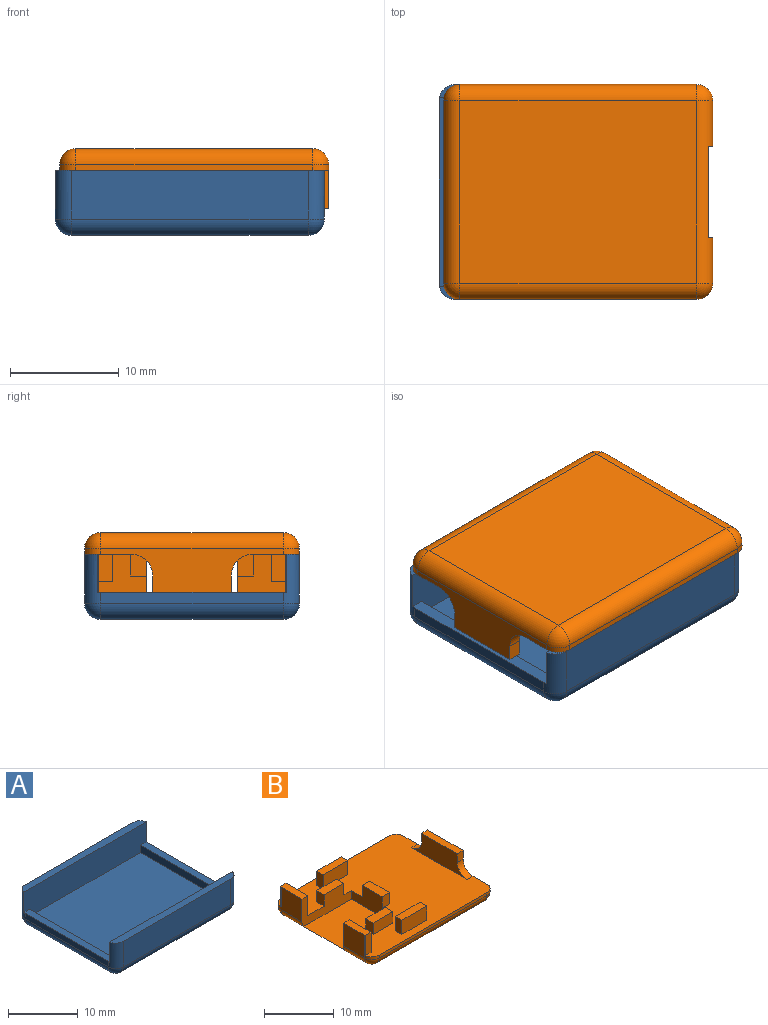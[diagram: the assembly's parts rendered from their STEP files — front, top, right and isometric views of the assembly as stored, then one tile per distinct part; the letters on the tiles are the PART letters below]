
ASSEMBLY  parts=2 mates=1
PART A: 26 faces, bbox 24.8x19.8x6 mm
  f0: plane 24.74x1.2mm, normal (0,0,1), area 28.8mm2, adj f4,f10,f14,f19
  f1: plane 16.8x1mm, normal (1,0,0), area 16.8mm2, adj f13,f19,f23,f25
  f2: plane 21.8x4.5mm, normal (0,1,0), area 98.1mm2, adj f5,f16,f22,f25
  f3: plane 16.8x1mm, normal (-1,0,0), area 16.8mm2, adj f12,f14,f16,f17
  f4: plane 21.8x4.5mm, normal (0,-1,0), area 98.1mm2, adj f0,f14,f18,f19
  f5: plane 24.74x1.2mm, normal (0,0,1), area 28.8mm2, adj f2,f8,f16,f25
  f6: plane 21.8x16.8mm, normal (0,0,-1), area 366.2mm2, adj f17,f18,f22,f23
  f7: plane 17.4x1.3mm, normal (-1,0,0), area 22.6mm2, adj f8,f10,f11,f13
  f8: plane 24.74x4.8mm, normal (0,-1,0), area 115.7mm2, adj f5,f7,f9,f11,f12,f13,f16,f25
  f9: plane 17.4x1.3mm, normal (1,0,0), area 22.6mm2, adj f8,f10,f11,f12
  f10: plane 24.74x4.8mm, normal (0,1,0), area 115.7mm2, adj f0,f7,f9,f11,f12,f13,f14,f19
  f11: plane 22.4x17.4mm, normal (0,0,1), area 389.8mm2, adj f7,f8,f9,f10
  f12: plane 17.4x1.2mm, normal (0,0,1), area 20.9mm2, adj f3,f8,f9,f10,f14,f16
  f13: plane 17.4x1.2mm, normal (0,0,1), area 20.9mm2, adj f1,f7,f8,f10,f19,f25
  f14: cylinder r=1.5mm len=4.5mm, axis (0,0,-1), area 9.5mm2, adj f0,f3,f4,f10,f12,f15
  f15: sphere r=1.5mm, area 3.5mm2, adj f14,f17,f18
  f16: cylinder r=1.5mm len=4.5mm, axis (0,0,1), area 9.5mm2, adj f2,f3,f5,f8,f12,f20
  f17: cylinder r=1.5mm len=16.8mm, axis (0,-1,0), area 39.6mm2, adj f3,f6,f15,f20
  f18: cylinder r=1.5mm len=21.8mm, axis (1,0,0), area 51.4mm2, adj f4,f6,f15,f21
  f19: cylinder r=1.5mm len=4.5mm, axis (0,0,1), area 9.5mm2, adj f0,f1,f4,f10,f13,f21
  f20: sphere r=1.5mm, area 3.5mm2, adj f16,f17,f22
  f21: sphere r=1.5mm, area 3.5mm2, adj f18,f19,f23
  f22: cylinder r=1.5mm len=21.8mm, axis (-1,0,0), area 51.4mm2, adj f2,f6,f20,f24
  f23: cylinder r=1.5mm len=16.8mm, axis (0,1,0), area 39.6mm2, adj f1,f6,f21,f24
  f24: sphere r=1.5mm, area 3.5mm2, adj f22,f23,f25
  f25: cylinder r=1.5mm len=4.5mm, axis (0,0,-1), area 9.5mm2, adj f1,f2,f5,f8,f13,f24
PART B: 57 faces, bbox 24.8x19.8x5.5 mm
  f0: plane 24.79x19.8mm, normal (0,0,1), area 350.1mm2, adj f2,f3,f4,f5,f6,f9,f10,f11
  f1: plane 4.2x4mm, normal (-1,0,0), area 16.8mm2, adj f19,f22,f36,f39
  f2: plane 16.8x4mm, normal (1,0,0), area 35.3mm2, adj f0,f3,f26,f29,f30,f31,f40,f41
  f3: cylinder r=1.5mm len=1.5mm, axis (0,0,-1), area 1.2mm2, adj f0,f2,f6,f24
  f4: plane 11.2x3.5mm, normal (-1,0,0), area 26.9mm2, adj f0,f30,f31,f40,f41,f42
  f5: plane 21.8x0.5mm, normal (0,-1,0), area 10.9mm2, adj f0,f23,f27,f29
  f6: plane 21.8x0.5mm, normal (0,1,0), area 10.9mm2, adj f0,f3,f19,f21
  f7: plane 4.2x4mm, normal (-1,0,0), area 16.8mm2, adj f22,f23,f32,f35
  f8: plane 21.8x16.8mm, normal (0,0,-1), area 366.2mm2, adj f21,f22,f26,f27
  f9: plane 2.5x1.3mm, normal (1,0,0), area 3.2mm2, adj f0,f10,f12,f13
  f10: plane 5x2.5mm, normal (0,1,0), area 12.5mm2, adj f0,f9,f11,f13
  f11: plane 2.5x1.3mm, normal (-1,0,0), area 3.2mm2, adj f0,f10,f12,f13
  f12: plane 5x2.5mm, normal (0,-1,0), area 12.5mm2, adj f0,f9,f11,f13
  f13: plane 5x1.3mm, normal (0,0,1), area 6.5mm2, adj f9,f10,f11,f12
  f14: plane 2.5x1.3mm, normal (-1,0,0), area 3.2mm2, adj f0,f15,f17,f18
  f15: plane 5x2.5mm, normal (0,-1,0), area 12.5mm2, adj f0,f14,f16,f18
  f16: plane 2.5x1.3mm, normal (1,0,0), area 3.2mm2, adj f0,f15,f17,f18
  f17: plane 5x2.5mm, normal (0,1,0), area 12.5mm2, adj f0,f14,f16,f18
  f18: plane 5x1.3mm, normal (0,0,1), area 6.5mm2, adj f14,f15,f16,f17
  f19: cylinder r=1.5mm len=4mm, axis (0,0,1), area 1.9mm2, adj f0,f1,f6,f20,f38,f39
  f20: sphere r=1.5mm, area 3.5mm2, adj f19,f21,f22
  f21: cylinder r=1.5mm len=21.8mm, axis (-1,0,0), area 51.4mm2, adj f6,f8,f20,f24
  f22: cylinder r=1.5mm len=16.8mm, axis (0,-1,0), area 30.4mm2, adj f1,f7,f8,f20,f25,f32,f36,f44
  f23: cylinder r=1.5mm len=4mm, axis (0,0,-1), area 1.9mm2, adj f0,f5,f7,f25,f33,f35
  f24: sphere r=1.5mm, area 3.5mm2, adj f3,f21,f26
  f25: sphere r=1.5mm, area 3.5mm2, adj f22,f23,f27
  f26: cylinder r=1.5mm len=16.8mm, axis (0,1,0), area 39.6mm2, adj f2,f8,f24,f28
  f27: cylinder r=1.5mm len=21.8mm, axis (1,0,0), area 51.4mm2, adj f5,f8,f25,f28
  f28: sphere r=1.5mm, area 3.5mm2, adj f26,f27,f29
  f29: cylinder r=1.5mm len=1.5mm, axis (0,0,1), area 1.2mm2, adj f0,f2,f5,f28
  f30: cylinder r=2mm len=2mm, axis (1,0,0), area 3.8mm2, adj f0,f2,f4,f40
  f31: cylinder r=2mm len=2mm, axis (1,0,0), area 3.8mm2, adj f0,f2,f4,f41
  f32: plane 10x5mm, normal (0,1,0), area 27.1mm2, adj f0,f7,f22,f34,f35,f43,f44,f45
  f33: plane 3.5x1.19mm, normal (0,-1,0), area 4.2mm2, adj f0,f23,f34,f35
  f34: plane 4.4x3.5mm, normal (1,0,0), area 15.4mm2, adj f0,f32,f33,f35
  f35: plane 4.4x1.2mm, normal (0,0,1), area 5.3mm2, adj f7,f23,f32,f33,f34
  f36: plane 10x5mm, normal (0,-1,0), area 27.1mm2, adj f0,f1,f22,f37,f39,f43,f44,f53
  f37: plane 4.4x3.5mm, normal (1,0,0), area 15.4mm2, adj f0,f36,f38,f39
  f38: plane 3.5x1.19mm, normal (0,1,0), area 4.2mm2, adj f0,f19,f37,f39
  f39: plane 4.4x1.2mm, normal (0,0,1), area 5.3mm2, adj f1,f19,f36,f37,f38
  f40: plane 1.5x1.2mm, normal (0,1,0), area 1.8mm2, adj f2,f4,f30,f42
  f41: plane 1.5x1.2mm, normal (0,-1,0), area 1.8mm2, adj f2,f4,f31,f42
  f42: plane 7.2x1.2mm, normal (0,0,1), area 8.6mm2, adj f2,f4,f40,f41
  f43: plane 8.4x3.5mm, normal (-1,0,0), area 20.6mm2, adj f0,f32,f36,f44,f49,f50,f52
  f44: plane 9.62x8.4mm, normal (0,0,1), area 80.8mm2, adj f22,f32,f36,f43
  f45: plane 2x1.5mm, normal (-1,0,0), area 3mm2, adj f0,f32,f46,f48
  f46: plane 4x2mm, normal (0,-1,0), area 8mm2, adj f0,f45,f47,f48
  f47: plane 2x1.5mm, normal (1,0,0), area 3mm2, adj f0,f32,f46,f48
  f48: plane 4x1.5mm, normal (0,0,1), area 6mm2, adj f32,f45,f46,f47
  f49: plane 2x1.5mm, normal (0,1,0), area 3mm2, adj f0,f43,f51,f52
  f50: plane 2x1.5mm, normal (0,-1,0), area 3mm2, adj f0,f43,f51,f52
  f51: plane 4x2mm, normal (1,0,0), area 8mm2, adj f0,f49,f50,f52
  f52: plane 4x1.5mm, normal (0,0,1), area 6mm2, adj f43,f49,f50,f51
  f53: plane 2x1.5mm, normal (1,0,0), area 3mm2, adj f0,f36,f54,f56
  f54: plane 4x2mm, normal (0,1,0), area 8mm2, adj f0,f53,f55,f56
  f55: plane 2x1.5mm, normal (-1,0,0), area 3mm2, adj f0,f36,f54,f56
  f56: plane 4x1.5mm, normal (0,0,1), area 6mm2, adj f36,f53,f54,f55
PLACE A t=(-8.93,-2.31,1.26)mm fixed
PLACE B rot(axis=(0,1,0),180deg) t=(-8.53,-2.31,9.26)mm
MATE parallel A.f11 <-> B.f0  axis (0,0,1) through (-8.93,-2.31,2.46)mm
